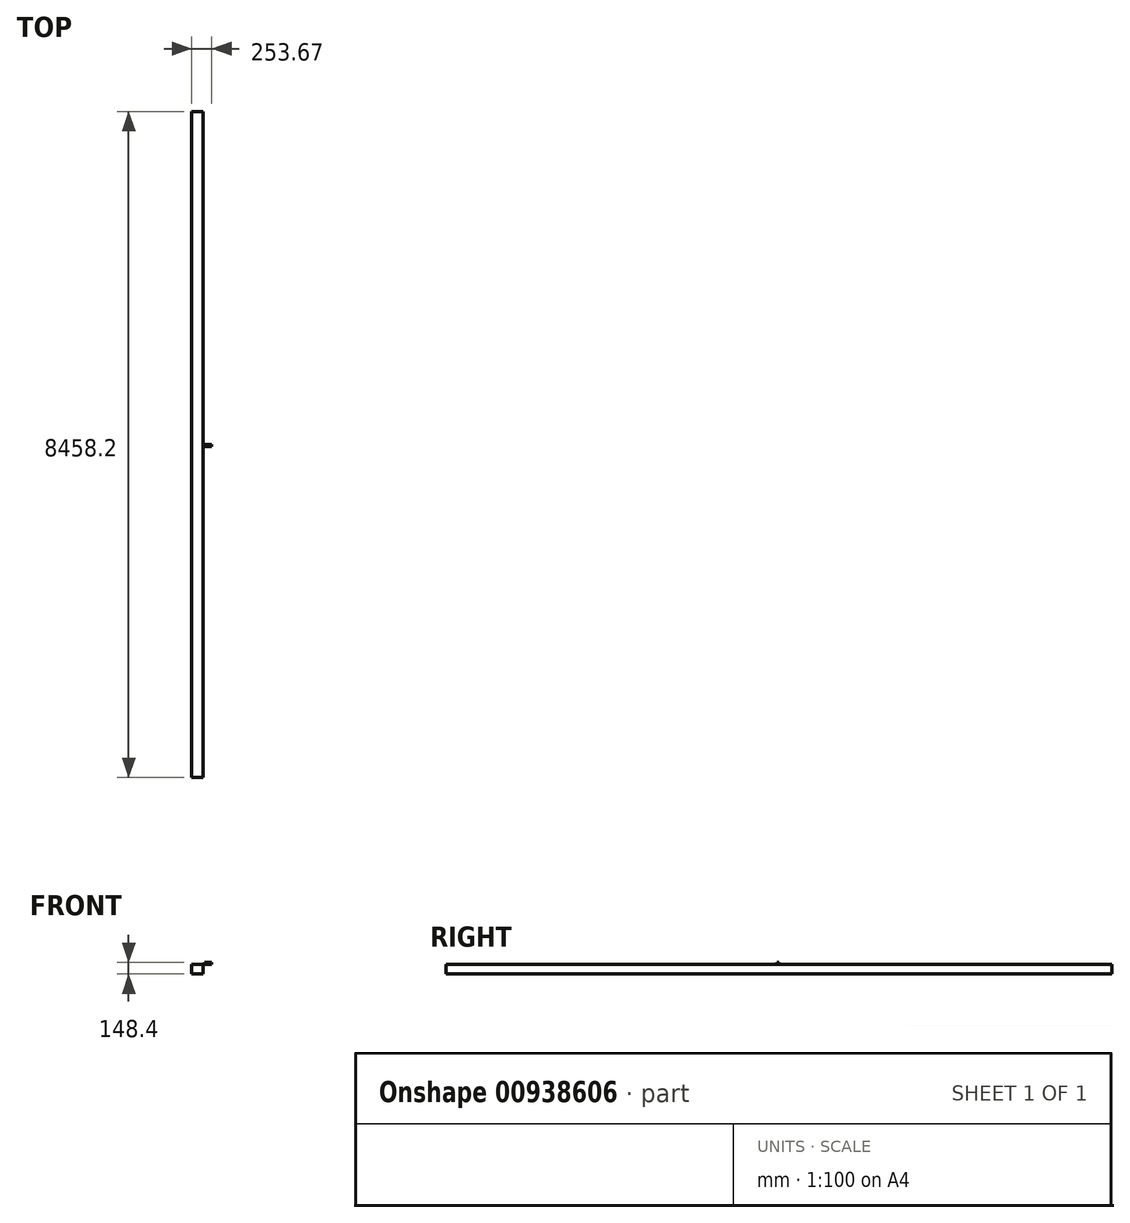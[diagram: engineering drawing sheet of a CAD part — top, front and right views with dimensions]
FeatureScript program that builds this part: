
annotation { "Feature Type Name" : "Feature", "Feature Type Description" : "" }
export const myFeature = defineFeature(function(context is Context, id is Id, definition is map)
    precondition{}
    {
        {
            var Q0;
            Q0=qCreatedBy(makeId("Front.planeOp"),FACE);
            var sketch = newSketch(context, id + "F0", { "sketchPlane" : qUnion([Q0])});
            skLineSegment(sketch, "E0.bottom", {"start": v(0, 0) * mm, "end": v(-2.33, 0) * mm});
            skLineSegment(sketch, "E0.top", {"start": v(0, -3.33) * mm, "end": v(-2.33, -3.33) * mm});
            skLineSegment(sketch, "E0.left", {"start": v(0, 0) * mm, "end": v(0, -3.33) * mm});
            skLineSegment(sketch, "E0.right", {"start": v(-2.33, 0) * mm, "end": v(-2.33, -3.33) * mm});
            skFitSpline(sketch, "E1", {"points": [v(-2.33, 0) * mm, v(-281.73, 0) * mm], "startDerivative": vector(-45.2, 0) * mm, "endDerivative": vector(-45.2, 0) * mm});
            skLineSegment(sketch, "E2.bottom", {"start": v(-17.4, 0) * mm, "end": v(-160.92, 0) * mm});
            skLineSegment(sketch, "E2.top", {"start": v(-17.4, -123) * mm, "end": v(-160.92, -123) * mm});
            skLineSegment(sketch, "E2.left", {"start": v(-17.4, 0) * mm, "end": v(-17.4, -123) * mm});
            skLineSegment(sketch, "E2.right", {"start": v(-160.92, 0) * mm, "end": v(-160.92, -123) * mm});
            skSolve(sketch);
        }
        {
            var Q0;
            Q0=makeQuery(id+"F0.imprint","IMPRINT",FACE,{"disambiguationData":[TD([[makeQuery(id+"F0.imprint","IMPRINT",EDGE,{"derivedFrom":sQuery(id+"F0.wireOp",EDGE,"E2.top")}),-1.0]])]});
            extrude(context, id + "F1", {"entities" : qUnion([Q0]), "endBound" : BoundingType.SYMMETRIC, "depth" : 8458.2 * mm, "offsetDistance" : 25.4 * mm});
        }
        {
            var Q0;
            Q0=qCreatedBy(makeId("Top.planeOp"),FACE);
            var sketch = newSketch(context, id + "F2", { "sketchPlane" : qUnion([Q0])});
            skLineSegment(sketch, "E3.bottom", {"start": v(0, 0) * mm, "end": v(92.75, 0) * mm});
            skLineSegment(sketch, "E3.top", {"start": v(0, -25.87) * mm, "end": v(92.75, -25.87) * mm});
            skLineSegment(sketch, "E3.left", {"start": v(0, 0) * mm, "end": v(0, -25.87) * mm});
            skLineSegment(sketch, "E3.right", {"start": v(92.75, 0) * mm, "end": v(92.75, -25.87) * mm});
            skSolve(sketch);
        }
        {
            var Q0;
            Q0=makeQuery(id+"F2.imprint","IMPRINT",FACE,{"disambiguationData":[TD([[makeQuery(id+"F2.imprint","IMPRINT",EDGE,{"derivedFrom":sQuery(id+"F2.wireOp",EDGE,"E3.bottom")}),-1.0]])]});
            extrude(context, id + "F3", {"entities" : qUnion([Q0]), "depth" : 25.4 * mm, "offsetDistance" : 25.4 * mm});
        }
    });
